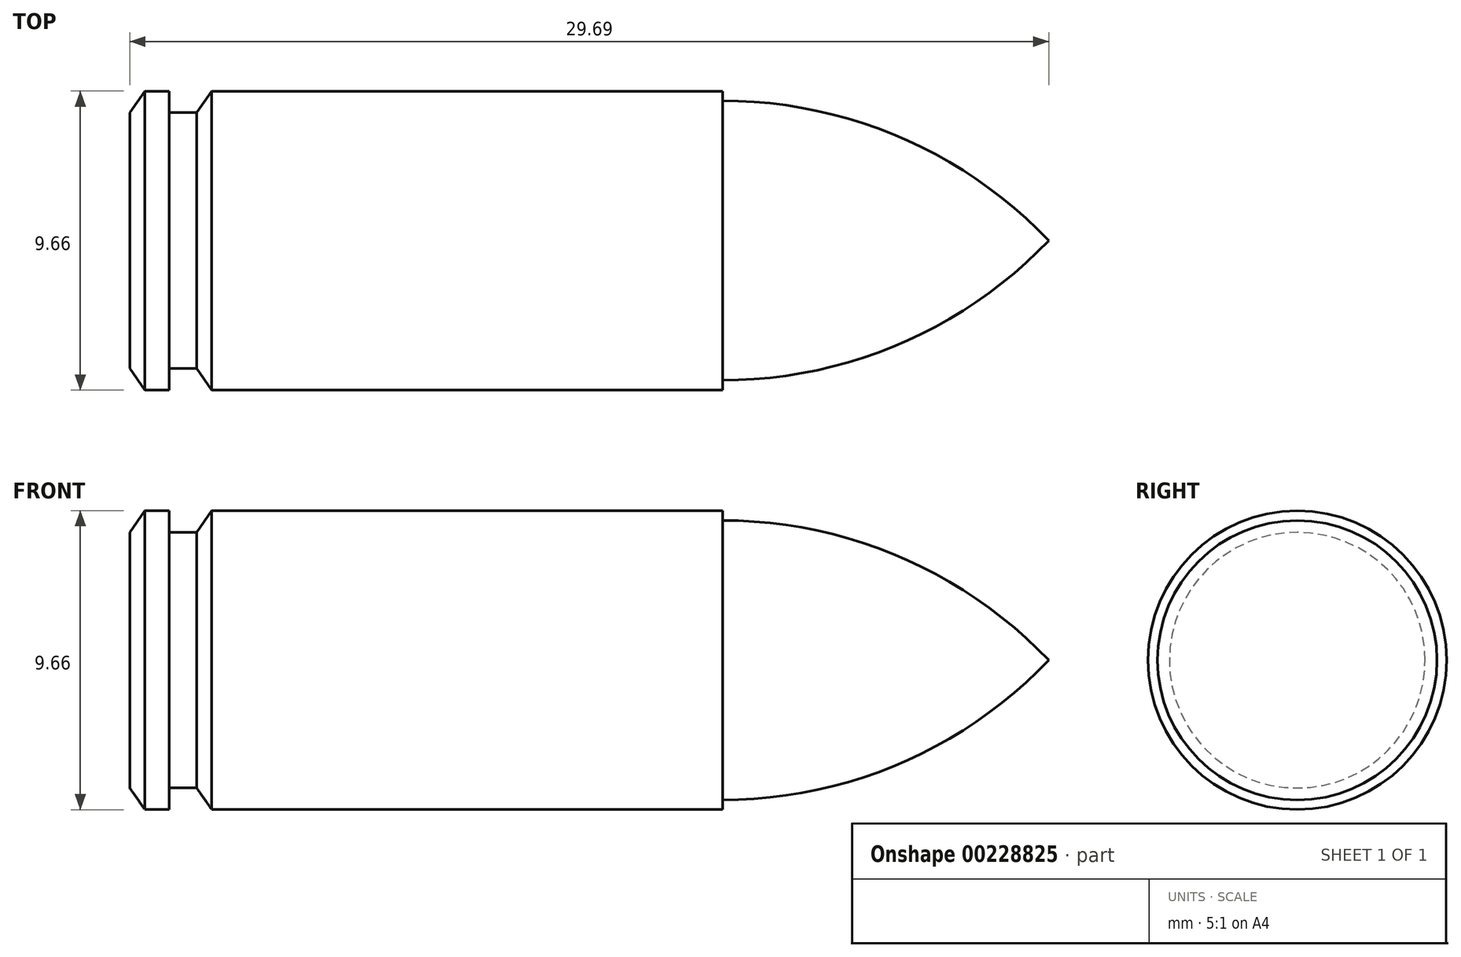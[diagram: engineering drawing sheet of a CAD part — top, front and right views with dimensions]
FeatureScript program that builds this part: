
annotation { "Feature Type Name" : "Feature", "Feature Type Description" : "" }
export const myFeature = defineFeature(function(context is Context, id is Id, definition is map)
    precondition{}
    {
        {
            var Q0;
            Q0=qCreatedBy(makeId("Front.planeOp"),FACE);
            var sketch = newSketch(context, id + "F0", { "sketchPlane" : qUnion([Q0])});
            skLineSegment(sketch, "E0.bottom", {"start": v(1.27, 4.83) * mm, "end": v(0.49, 4.83) * mm});
            skLineSegment(sketch, "E0.top", {"start": v(1.27, 0) * mm, "end": v(0, 0) * mm});
            skLineSegment(sketch, "E0.left", {"start": v(1.27, 4.83) * mm, "end": v(1.27, 0) * mm});
            skLineSegment(sketch, "E0.right", {"start": v(0, 4.13) * mm, "end": v(0, 0) * mm});
            skLineSegment(sketch, "E1", {"start": v(0, 4.13) * mm, "end": v(0.49, 4.83) * mm});
            skLineSegment(sketch, "E2.bottom", {"start": v(1.27, 4.13) * mm, "end": v(2.16, 4.13) * mm});
            skLineSegment(sketch, "E2.top", {"start": v(1.27, 0) * mm, "end": v(2.16, 0) * mm});
            skLineSegment(sketch, "E2.left", {"start": v(1.27, 4.13) * mm, "end": v(1.27, 0) * mm});
            skLineSegment(sketch, "E2.right", {"start": v(2.16, 4.13) * mm, "end": v(2.16, 0) * mm});
            skLineSegment(sketch, "E3", {"start": v(2.16, 4.13) * mm, "end": v(2.65, 4.83) * mm});
            skLineSegment(sketch, "E4", {"start": v(2.65, 4.83) * mm, "end": v(19.15, 4.83) * mm});
            skLineSegment(sketch, "E5", {"start": v(19.15, 4.83) * mm, "end": v(19.15, 0) * mm});
            skLineSegment(sketch, "E6", {"start": v(19.15, 0) * mm, "end": v(2.16, 0) * mm});
            skLineSegment(sketch, "E7", {"start": v(19.15, 0) * mm, "end": v(29.7, 0) * mm});
            skLineSegment(sketch, "E8.bottom", {"start": v(0, 4.51) * mm, "end": v(29.7, 4.51) * mm, "construction": true});
            skLineSegment(sketch, "E8.top", {"start": v(0, 0) * mm, "end": v(29.7, 0) * mm, "construction": true});
            skLineSegment(sketch, "E8.left", {"start": v(0, 4.51) * mm, "end": v(0, 0) * mm, "construction": true});
            skLineSegment(sketch, "E8.right", {"start": v(29.7, 4.51) * mm, "end": v(29.7, 0) * mm, "construction": true});
            skArc(sketch, "E9", {"start": v(29.7, 0) * mm, "mid": v(24.88, 3.34) * mm, "end": v(19.15, 4.51) * mm});
            skSolve(sketch);
        }
        {
            var Q0;
            {var subQ0=sQuery(id+"F0.wireOp",EDGE,"E7");Q0=makeQuery(id+"F0.imprint","IMPRINT",FACE,{"disambiguationData":[TD([[makeQuery(id+"F0.imprint","IMPRINT",EDGE,{"derivedFrom":subQ0}),1.0]])]});}
            var Q1;
            Q1=makeQuery(id+"F0.imprint","IMPRINT",FACE,{"disambiguationData":[TD([[makeQuery(id+"F0.imprint","IMPRINT",EDGE,{"derivedFrom":sQuery(id+"F0.wireOp",EDGE,"E2.right")}),1.0]])]});
            var Q2;
            Q2=makeQuery(id+"F0.imprint","IMPRINT",FACE,{"disambiguationData":[TD([[makeQuery(id+"F0.imprint","IMPRINT",EDGE,{"derivedFrom":sQuery(id+"F0.wireOp",EDGE,"E2.bottom")}),-1.0]])]});
            var Q3;
            Q3=makeQuery(id+"F0.imprint","IMPRINT",FACE,{"disambiguationData":[TD([[makeQuery(id+"F0.imprint","IMPRINT",EDGE,{"derivedFrom":sQuery(id+"F0.wireOp",EDGE,"E0.bottom")}),1.0]])]});
            var Q4;
            Q4=sQuery(id+"F0.wireOp",EDGE,"E6");
            revolve(context, id + "F1", {"entities" : qUnion([Q0, Q1, Q2, Q3]), "axis" : qUnion([Q4]), "revolveType" : RevolveType.FULL});
        }
    });
